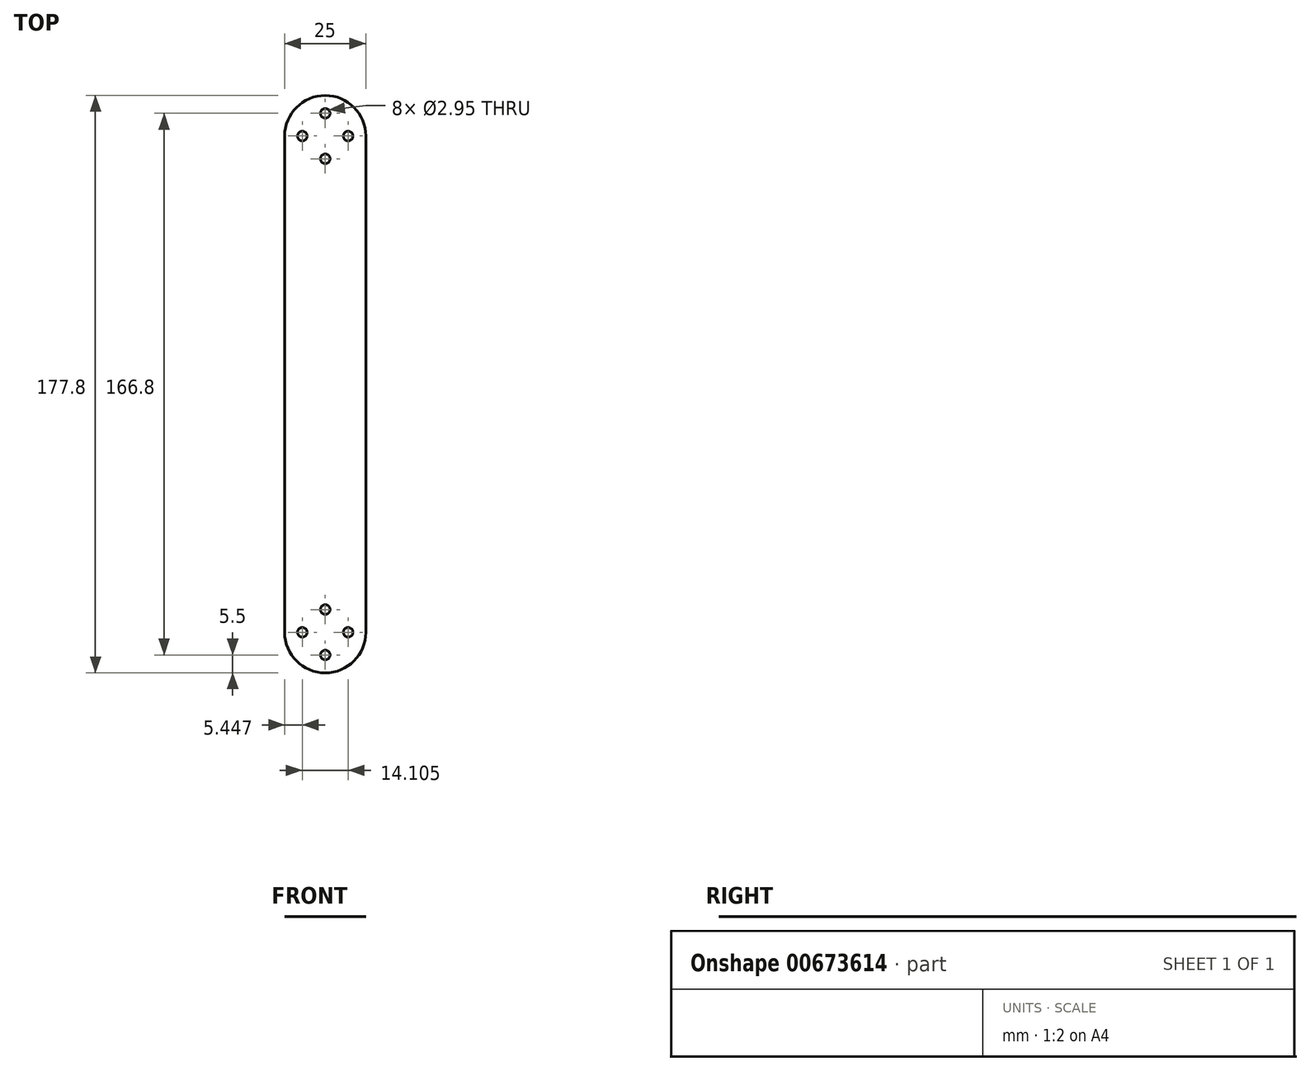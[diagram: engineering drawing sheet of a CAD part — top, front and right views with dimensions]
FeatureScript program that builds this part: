
annotation { "Feature Type Name" : "Feature", "Feature Type Description" : "" }
export const myFeature = defineFeature(function(context is Context, id is Id, definition is map)
    precondition{}
    {
        {
            var Q0;
            Q0=qCreatedBy(makeId("Top.planeOp"),FACE);
            var sketch = newSketch(context, id + "F0", { "sketchPlane" : qUnion([Q0])});
            skLineSegment(sketch, "E0.bottom", {"start": v(0, 88.9) * mm, "end": v(0, 88.9) * mm});
            skLineSegment(sketch, "E0.top", {"start": v(0, -88.9) * mm, "end": v(0, -88.9) * mm});
            skLineSegment(sketch, "E0.left", {"start": v(12.5, 76.4) * mm, "end": v(12.5, -76.4) * mm});
            skLineSegment(sketch, "E0.right", {"start": v(-12.5, 76.4) * mm, "end": v(-12.5, -76.4) * mm});
            skPoint(sketch, "E0.middle", {"position": v(0, 0) * mm});
            skPoint(sketch, "E1.visualSharp", {"position": v(12.5, 88.9) * mm});
            skArc(sketch, "E1.filletArc", {"start": v(12.5, 76.4) * mm, "mid": v(8.84, 85.24) * mm, "end": v(0, 88.9) * mm});
            skPoint(sketch, "E2.visualSharp", {"position": v(-12.5, 88.9) * mm});
            skArc(sketch, "E2.filletArc", {"start": v(0, 88.9) * mm, "mid": v(-8.84, 85.24) * mm, "end": v(-12.5, 76.4) * mm});
            skPoint(sketch, "E3.visualSharp", {"position": v(-12.5, -88.9) * mm});
            skArc(sketch, "E3.filletArc", {"start": v(-12.5, -76.4) * mm, "mid": v(-8.84, -85.24) * mm, "end": v(0, -88.9) * mm});
            skPoint(sketch, "E4.visualSharp", {"position": v(12.5, -88.9) * mm});
            skArc(sketch, "E4.filletArc", {"start": v(0, -88.9) * mm, "mid": v(8.84, -85.24) * mm, "end": v(12.5, -76.4) * mm});
            skCircle(sketch, "E5", {"center": v(0, 76.4) * mm, "radius": 10 * mm, "construction": true});
            skCircle(sketch, "E6", {"center": v(0, 83.4) * mm, "radius": 1.47 * mm});
            skCircle(sketch, "E7", {"center": v(0, 69.4) * mm, "radius": 1.47 * mm});
            skLineSegment(sketch, "E8", {"start": v(0, 83.4) * mm, "end": v(0, 76.4) * mm, "construction": true});
            skLineSegment(sketch, "E9", {"start": v(0, 76.4) * mm, "end": v(0, 69.4) * mm, "construction": true});
            skCircle(sketch, "E10", {"center": v(7.05, 76.4) * mm, "radius": 1.47 * mm});
            skCircle(sketch, "E11", {"center": v(-7.05, 76.4) * mm, "radius": 1.47 * mm});
            skLineSegment(sketch, "E12", {"start": v(0, 76.4) * mm, "end": v(7.05, 76.4) * mm, "construction": true});
            skLineSegment(sketch, "E13", {"start": v(-7.05, 76.4) * mm, "end": v(0, 76.4) * mm, "construction": true});
            skLineSegment(sketch, "E14", {"start": v(-12.5, 0) * mm, "end": v(12.5, 0) * mm, "construction": true});
            skCircle(sketch, "E15.MirrorC", {"center": v(-7.05, -76.4) * mm, "radius": 1.47 * mm});
            skCircle(sketch, "E16.MirrorC", {"center": v(7.05, -76.4) * mm, "radius": 1.47 * mm});
            skCircle(sketch, "E17.MirrorC", {"center": v(0, -83.4) * mm, "radius": 1.47 * mm});
            skCircle(sketch, "E18.MirrorC", {"center": v(0, -76.4) * mm, "radius": 10 * mm, "construction": true});
            skCircle(sketch, "E19.MirrorC", {"center": v(0, -69.4) * mm, "radius": 1.47 * mm});
            skSolve(sketch);
        }
        {
            var Q0;
            Q0=makeQuery(id+"F0.imprint","IMPRINT",FACE,{"disambiguationData":[TD([[makeQuery(id+"F0.imprint","IMPRINT",EDGE,{"derivedFrom":sQuery(id+"F0.wireOp",EDGE,"E0.left")}),-1.0]])]});
            extrude(context, id + "F1", {"entities" : qUnion([Q0]), "depth" : 1 / 203.2 * mm});
        }
    });
